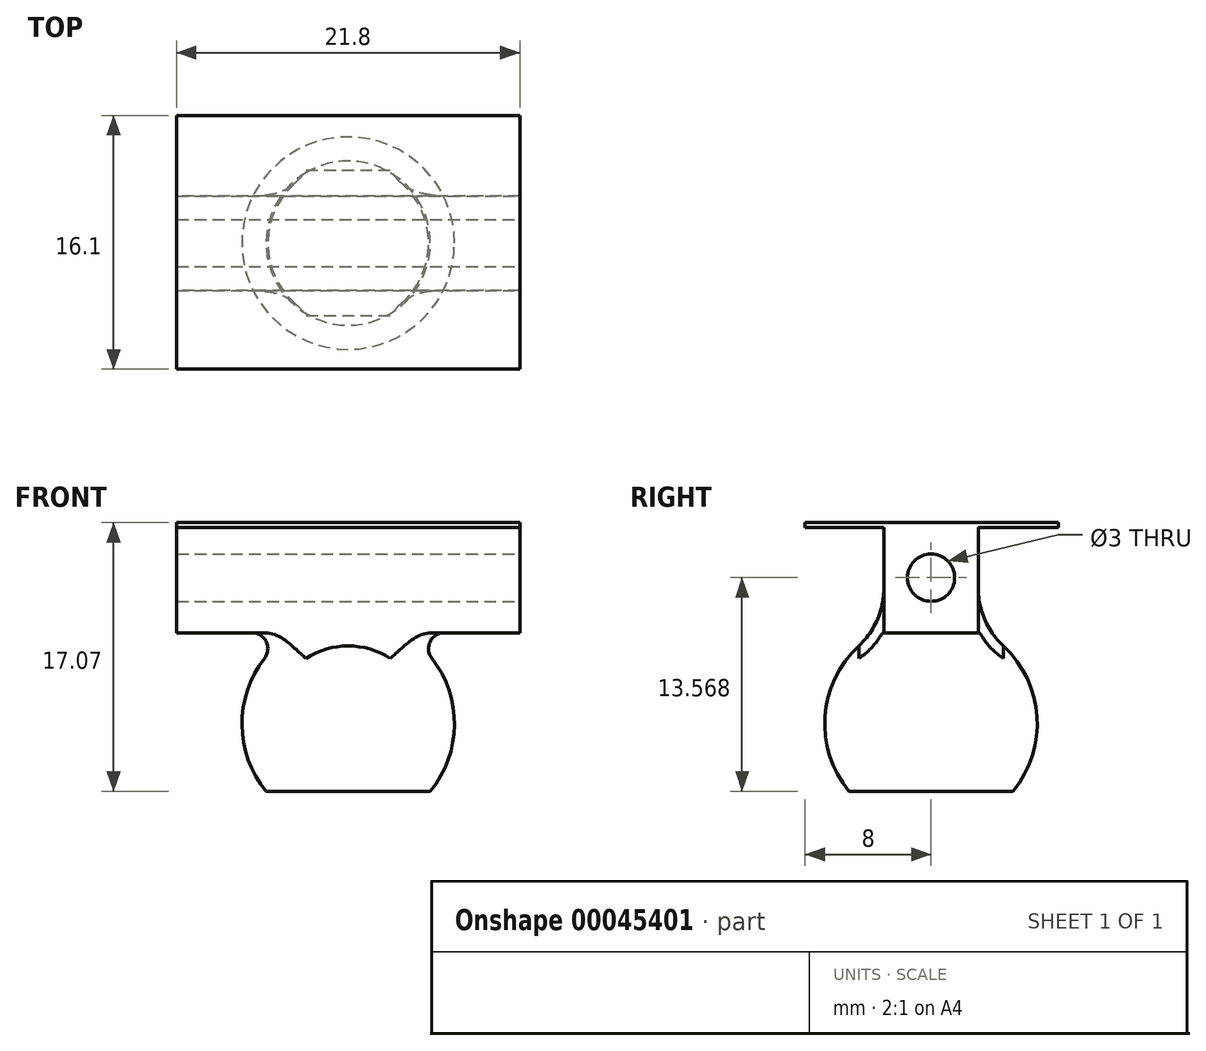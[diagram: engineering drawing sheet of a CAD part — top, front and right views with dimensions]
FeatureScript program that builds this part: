
annotation { "Feature Type Name" : "Feature", "Feature Type Description" : "" }
export const myFeature = defineFeature(function(context is Context, id is Id, definition is map)
    precondition{}
    {
        {
            var Q0;
            Q0=qCreatedBy(makeId("Front.planeOp"),FACE);
            var sketch = newSketch(context, id + "F0", { "sketchPlane" : qUnion([Q0])});
            skArc(sketch, "E0", {"start": v(-1.7, 6.53) * mm, "mid": v(-6.42, 2.08) * mm, "end": v(-5.21, -4.29) * mm});
            skLineSegment(sketch, "E1", {"start": v(0, 6.75) * mm, "end": v(0, -4.29) * mm});
            skLineSegment(sketch, "E2.bottom", {"start": v(0, 6.78) * mm, "end": v(-1.7, 6.78) * mm});
            skLineSegment(sketch, "E2.left", {"start": v(0, 6.78) * mm, "end": v(0, 6.75) * mm});
            skLineSegment(sketch, "E2.right", {"start": v(-1.7, 6.78) * mm, "end": v(-1.7, 6.53) * mm});
            skLineSegment(sketch, "E3", {"start": v(0, -4.29) * mm, "end": v(-5.21, -4.29) * mm});
            skSolve(sketch);
        }
        {
            var Q0;
            Q0=makeQuery(id+"F0.imprint","IMPRINT",FACE,{"disambiguationData":[TD([[makeQuery(id+"F0.imprint","IMPRINT",EDGE,{"derivedFrom":sQuery(id+"F0.wireOp",EDGE,"E0")}),1.0]])]});
            var Q1;
            Q1=sQuery(id+"F0.wireOp",EDGE,"E1");
            revolve(context, id + "F1", {"entities" : qUnion([Q0]), "axis" : qUnion([Q1]), "revolveType" : RevolveType.FULL});
        }
        {
            var Q0;
            Q0=makeQuery(id+"F1.opRevolve","SWEPT_FACE",FACE,{"disambiguationData":[OSD([sQuery(id+"F0.wireOp",EDGE,"E2.bottom")])]});
            var sketch = newSketch(context, id + "F2", { "sketchPlane" : qUnion([Q0])});
            skLineSegment(sketch, "E4.bottom", {"start": v(-10.9, 3) * mm, "end": v(10.9, 3) * mm});
            skLineSegment(sketch, "E4.top", {"start": v(-10.9, -3) * mm, "end": v(10.9, -3) * mm});
            skLineSegment(sketch, "E4.left", {"start": v(-10.9, 3) * mm, "end": v(-10.9, -3) * mm});
            skLineSegment(sketch, "E4.right", {"start": v(10.9, 3) * mm, "end": v(10.9, -3) * mm});
            skLineSegment(sketch, "E5", {"start": v(0, 0) * mm, "end": v(-6.5, 0) * mm, "construction": true});
            skLineSegment(sketch, "E6", {"start": v(0, 0) * mm, "end": v(0, 3.68) * mm, "construction": true});
            skSolve(sketch);
        }
        {
            var Q0;
            Q0=makeQuery(id+"F2.imprint","IMPRINT",FACE,{"disambiguationData":[TD([[makeQuery(id+"F2.imprint","IMPRINT",EDGE,{"derivedFrom":makeQuery(id+"F1.opRevolve","SWEPT_EDGE",EDGE,{"disambiguationData":[OSD([sQuery(id+"F0.wireOp",EDGE,"E2.bottom"),sQuery(id+"F0.wireOp",EDGE,"E2.right")])]})}),1.0]])]});
            var Q1;
            Q1=makeQuery(id+"F2.imprint","IMPRINT",FACE,{"disambiguationData":[TD([[makeQuery(id+"F2.imprint","IMPRINT",EDGE,{"derivedFrom":sQuery(id+"F2.wireOp",EDGE,"E4.bottom")}),-1.0]])]});
            extrude(context, id + "F3", {"entities" : qUnion([Q0, Q1]), "operationType" : NewBodyOperationType.ADD, "depth" : 6 * mm, "hasSecondDirection" : true, "secondDirectionOppositeDirection" : true, "secondDirectionDepth" : 1 * mm});
        }
        {
            var Q0;
            Q0=makeQuery(id+"F3.opExtrude","SWEPT_FACE",FACE,{"disambiguationData":[OSD([sQuery(id+"F2.wireOp",EDGE,"E4.right")])]});
            var sketch = newSketch(context, id + "F4", { "sketchPlane" : qUnion([Q0])});
            skLineSegment(sketch, "E7", {"start": v(0, 12.78) * mm, "end": v(0, 5.78) * mm, "construction": true});
            skLineSegment(sketch, "E8", {"start": v(-3, 9.28) * mm, "end": v(3, 9.28) * mm, "construction": true});
            skCircle(sketch, "E9", {"center": v(0, 9.28) * mm, "radius": 1.5 * mm});
            skSolve(sketch);
        }
        {
            var Q0;
            Q0=makeQuery(id+"F4.imprint","IMPRINT",FACE,{"disambiguationData":[TD([[makeQuery(id+"F4.imprint","IMPRINT",EDGE,{"derivedFrom":sQuery(id+"F4.wireOp",EDGE,"E9")}),1.0]])]});
            extrude(context, id + "F5", {"entities" : qUnion([Q0]), "operationType" : NewBodyOperationType.REMOVE, "oppositeDirection" : true, "depth" : 25 * mm});
        }
        {
            var Q0;
            Q0=makeQuery(id+"F3.boolean.opBoolean","INTERSECT",EDGE,{"disambiguationData":[OD(0.0)],"derivedFrom":[makeQuery(id+"F1.opRevolve","SWEPT_FACE",FACE,{"disambiguationData":[OSD([sQuery(id+"F0.wireOp",EDGE,"E0")])]}),makeQuery(id+"F3.opExtrude","CAP_FACE",FACE,{"disambiguationData":[OSD([sQuery(id+"F2.wireOp",EDGE,"E4.bottom"),sQuery(id+"F2.wireOp",EDGE,"E4.top"),sQuery(id+"F2.wireOp",EDGE,"E4.left"),sQuery(id+"F2.wireOp",EDGE,"E4.right")])],"isStart":true})]});
            var Q1;
            Q1=makeQuery(id+"F3.boolean.opBoolean","INTERSECT",EDGE,{"disambiguationData":[OD(1.0)],"derivedFrom":[makeQuery(id+"F1.opRevolve","SWEPT_FACE",FACE,{"disambiguationData":[OSD([sQuery(id+"F0.wireOp",EDGE,"E0")])]}),makeQuery(id+"F3.opExtrude","CAP_FACE",FACE,{"disambiguationData":[OSD([sQuery(id+"F2.wireOp",EDGE,"E4.bottom"),sQuery(id+"F2.wireOp",EDGE,"E4.top"),sQuery(id+"F2.wireOp",EDGE,"E4.left"),sQuery(id+"F2.wireOp",EDGE,"E4.right")])],"isStart":true})]});
            fillet(context, id + "F6", {"entities" : qUnion([Q0, Q1]), "radius" : 1 * mm, "tangentPropagation" : true, "allowEdgeOverflow" : false});
        }
        {
            var Q0;
            Q0=makeQuery(id+"F3.boolean.opBoolean","INTERSECT",EDGE,{"derivedFrom":[makeQuery(id+"F1.opRevolve","SWEPT_FACE",FACE,{"disambiguationData":[OSD([sQuery(id+"F0.wireOp",EDGE,"E0")])]}),makeQuery(id+"F3.opExtrude","SWEPT_FACE",FACE,{"disambiguationData":[OSD([sQuery(id+"F2.wireOp",EDGE,"E4.top")])]})]});
            var Q1;
            Q1=makeQuery(id+"F3.boolean.opBoolean","INTERSECT",EDGE,{"derivedFrom":[makeQuery(id+"F1.opRevolve","SWEPT_FACE",FACE,{"disambiguationData":[OSD([sQuery(id+"F0.wireOp",EDGE,"E0")])]}),makeQuery(id+"F3.opExtrude","SWEPT_FACE",FACE,{"disambiguationData":[OSD([sQuery(id+"F2.wireOp",EDGE,"E4.bottom")])]})]});
            fillet(context, id + "F7", {"entities" : qUnion([Q0, Q1]), "radius" : 5 * mm, "tangentPropagation" : true, "allowEdgeOverflow" : false});
        }
        {
            var Q0;
            Q0=makeQuery(id+"F3.opExtrude","SWEPT_FACE",FACE,{"disambiguationData":[OSD([sQuery(id+"F2.wireOp",EDGE,"E4.bottom")])]});
            var sketch = newSketch(context, id + "F8", { "sketchPlane" : qUnion([Q0])});
            skLineSegment(sketch, "E10.bottom", {"start": v(-10.9, 12.78) * mm, "end": v(10.9, 12.78) * mm});
            skLineSegment(sketch, "E10.top", {"start": v(-10.9, 12.48) * mm, "end": v(10.9, 12.48) * mm});
            skLineSegment(sketch, "E10.left", {"start": v(-10.9, 12.78) * mm, "end": v(-10.9, 12.48) * mm});
            skLineSegment(sketch, "E10.right", {"start": v(10.9, 12.78) * mm, "end": v(10.9, 12.48) * mm});
            skSolve(sketch);
        }
        {
            var Q0;
            Q0=makeQuery(id+"F3.opExtrude","SWEPT_FACE",FACE,{"disambiguationData":[OSD([sQuery(id+"F2.wireOp",EDGE,"E4.top")])]});
            var sketch = newSketch(context, id + "F9", { "sketchPlane" : qUnion([Q0])});
            skLineSegment(sketch, "E11.bottom", {"start": v(-10.9, 12.78) * mm, "end": v(10.9, 12.78) * mm});
            skLineSegment(sketch, "E11.top", {"start": v(-10.9, 12.48) * mm, "end": v(10.9, 12.48) * mm});
            skLineSegment(sketch, "E11.left", {"start": v(-10.9, 12.78) * mm, "end": v(-10.9, 12.48) * mm});
            skLineSegment(sketch, "E11.right", {"start": v(10.9, 12.78) * mm, "end": v(10.9, 12.48) * mm});
            skSolve(sketch);
        }
        {
            var Q0;
            Q0=makeQuery(id+"F9.imprint","IMPRINT",FACE,{"disambiguationData":[TD([[makeQuery(id+"F9.imprint","IMPRINT",EDGE,{"derivedFrom":sQuery(id+"F9.wireOp",EDGE,"E11.bottom")}),-1.0]])]});
            var Q1;
            Q1=makeQuery(id+"F8.imprint","IMPRINT",FACE,{"disambiguationData":[TD([[makeQuery(id+"F8.imprint","IMPRINT",EDGE,{"derivedFrom":sQuery(id+"F8.wireOp",EDGE,"E10.bottom")}),1.0]])]});
            extrude(context, id + "F10", {"entities" : qUnion([Q0, Q1]), "operationType" : NewBodyOperationType.ADD, "depth" : 5 * mm, "hasSecondDirection" : true, "secondDirectionOppositeDirection" : true, "secondDirectionDepth" : 5.1 * mm});
        }
    });
